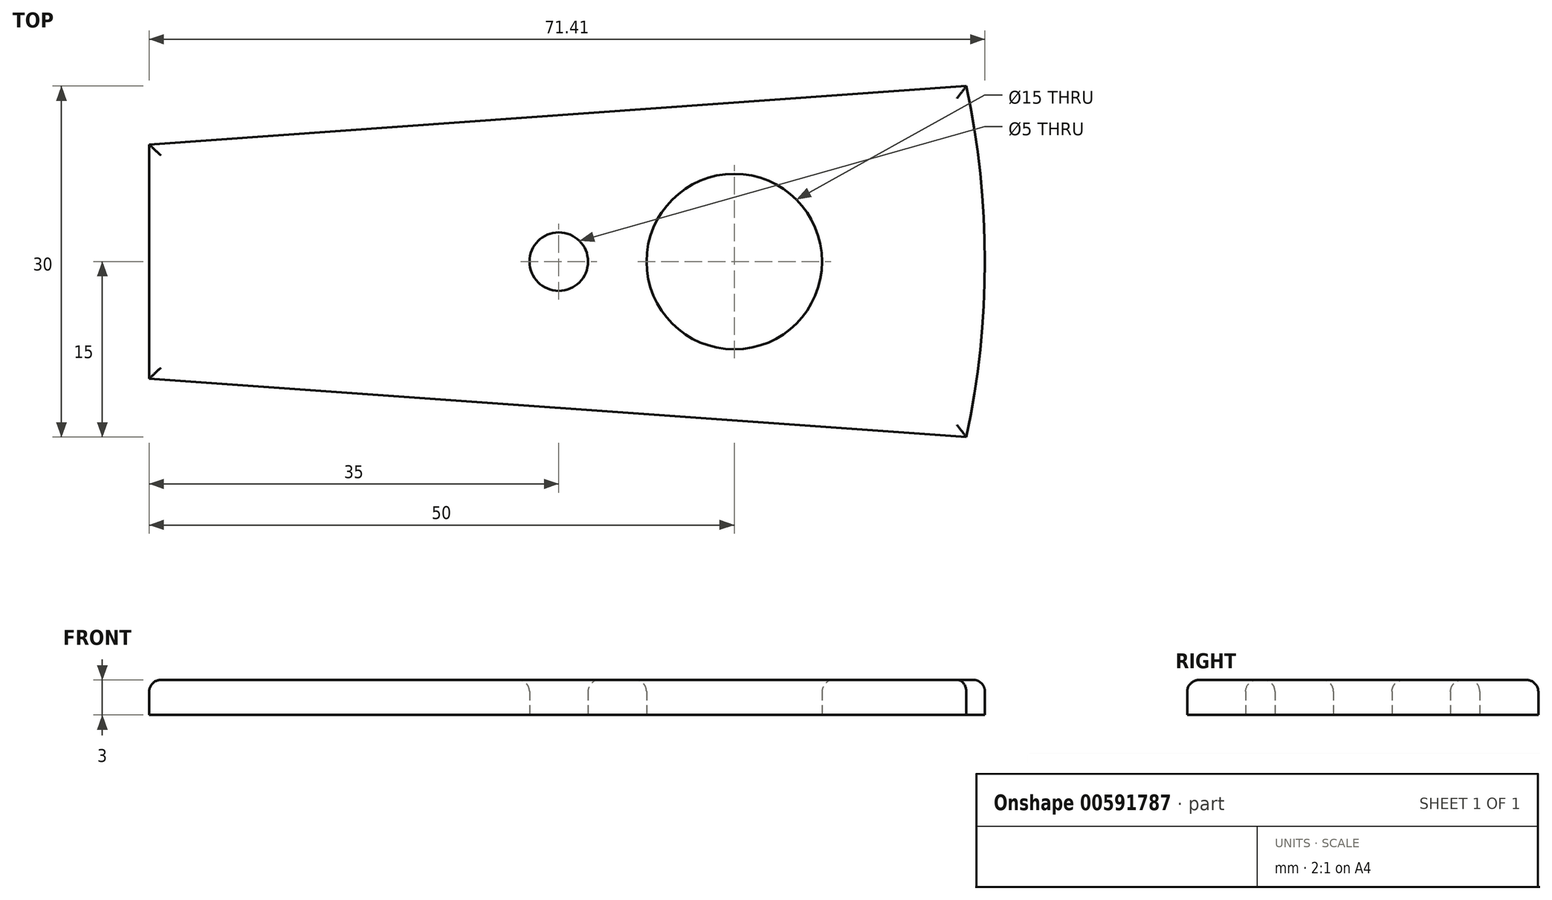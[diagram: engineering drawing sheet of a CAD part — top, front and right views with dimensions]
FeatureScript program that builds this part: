
annotation { "Feature Type Name" : "Feature", "Feature Type Description" : "" }
export const myFeature = defineFeature(function(context is Context, id is Id, definition is map)
    precondition{}
    {
        {
            var Q0;
            Q0=qCreatedBy(makeId("Top.planeOp"),FACE);
            var sketch = newSketch(context, id + "F0", { "sketchPlane" : qUnion([Q0])});
            skPoint(sketch, "E0", {"position": v(-35, 10) * mm});
            skPoint(sketch, "E1", {"position": v(-35, -10) * mm});
            skPoint(sketch, "E2", {"position": v(34.82, -15) * mm});
            skPoint(sketch, "E3", {"position": v(34.82, 15) * mm});
            skLineSegment(sketch, "E4", {"start": v(34.82, 15) * mm, "end": v(-35, 10) * mm});
            skLineSegment(sketch, "E5", {"start": v(-35, -10) * mm, "end": v(34.82, -15) * mm});
            skCircle(sketch, "E6", {"center": v(15, 0) * mm, "radius": 7.5 * mm});
            skCircle(sketch, "E7", {"center": v(0, 0) * mm, "radius": 2.5 * mm});
            skArc(sketch, "E8", {"start": v(34.82, 15) * mm, "mid": v(36.41, 0) * mm, "end": v(34.82, -15) * mm});
            skLineSegment(sketch, "E9", {"start": v(-35, -10) * mm, "end": v(-35, 10) * mm});
            skSolve(sketch);
        }
        {
            var Q0;
            Q0=makeQuery(id+"F0.imprint","IMPRINT",FACE,{"disambiguationData":[TD([[makeQuery(id+"F0.imprint","IMPRINT",EDGE,{"derivedFrom":sQuery(id+"F0.wireOp",EDGE,"E4")}),1.0]])]});
            extrude(context, id + "F1", {"entities" : qUnion([Q0]), "depth" : 3 * mm, "offsetDistance" : 25 * mm});
        }
        {
            var Q0;
            Q0=makeQuery(id+"F1.opExtrude","CAP_FACE",FACE,{"disambiguationData":[OSD([sQuery(id+"F0.wireOp",EDGE,"E4"),sQuery(id+"F0.wireOp",EDGE,"sVobcLzv-jP12-Rkn3-uBej-WuM4FMK0faFh"),sQuery(id+"F0.wireOp",EDGE,"E5"),sQuery(id+"F0.wireOp",EDGE,"4DMmSAuJ-Rn4V-lBEU-kwxr-sIgi4gKM6pwX"),sQuery(id+"F0.wireOp",EDGE,"E6"),sQuery(id+"F0.wireOp",EDGE,"E7")])],"isStart":false});
            fillet(context, id + "F2", {"entities" : qUnion([Q0]), "radius" : 1 * mm, "tangentPropagation" : true, "allowEdgeOverflow" : false});
        }
    });
